# Revit family: Haworth_X99_Chair_Seminar
name_source: partatom
category: Furniture
revit_build: Autodesk Revit 2018 (Build: 20170223_1515(x64)
units: mm (PartAtom-declared; Revit-internal decimal feet)

## family parameters
Always vertical = Yes
Cut with Voids When Loaded = No
OmniClass Number = 23.40.70.14.64.11
OmniClass Title = Office Furniture
Room Calculation Point = No
Shared = No
Work Plane-Based = No

## types (3) — shared parameters
Aluminum Base = Yes
Arm Armless = No
Arms Fixed = Yes
Assembly Code = E2020200
Back Cushion = No
Back Mesh = Yes
Back Upholstery Finish = Haworth _ Fabric _ Zinger _ Gravel NI-4
Base Finish = Haworth _ Metal _ Chrome
Description = Haworth - Chair - X99 - Seminar
Manufacturer = Haworth
Model = Haworth - Chair - X99 - Seminar
Revision Number = 2
Seat Finish = Haworth _ Fabric _ Zinger _ Gravel NI-4
Steel Base = No
Sustainability Info = http://www.haworth.com
URL = www.haworth.com
URL - Product = http://www.haworth.com
Warranty = http://www.haworth.com

## per-type parameters (varying)
| type | Casters | Five Star Base | Nested Base |
| X99 Seminar Chair with Caster | Yes | No | Yes |
| X99 Advanced Seminar Chair | No | Yes | No |
| X99 Seminar Chair with Glides | No | No | Yes |

## geometry (parser evidence)
native form markers: Sweep x14
no freeform markers — native parametric forms only
